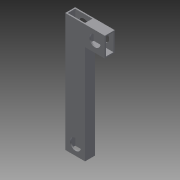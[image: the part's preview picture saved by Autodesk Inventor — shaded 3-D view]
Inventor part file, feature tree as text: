
AUTODESK INVENTOR PART (.ipt)
format: ipt  version: 2016 (Build 200138000, 138)  size: 128,000 bytes
history: native  units: in
note: dims shown in document units (in); Inventor stores cm internally (conversion verified against a paired STEP export)
features: extrude x5, sketch x5
ambient origin geometry x8: Origin, YZ Plane, XZ Plane, XY Plane, X Axis, Y Axis, Z Axis, Center Point
bodies: Solid1 (feature_tree)
feature tree (10):
  extrude  "Extrusion1"  Depth=1.0in
  extrude  "Extrusion2"  Depth=0.1253in
  extrude  "Extrusion3"  Depth=0.125in
  extrude  "Extrusion4"  Depth=2.0in
  extrude  "Extrusion5"  Depth=0.125in
  sketch  "Sketch1"  dims[d0=2.0in d1=1.0in]
  sketch  "Sketch2"  dims[d2=0.125in d3=0.1253in]
  sketch  "Sketch3"  dims[d4=0.125in d5=0.125in]
  sketch  "Sketch4"  dims[d6=12.0in d7=0.0in d8=2.0in]
  sketch  "Sketch5"  dims[d9=0.125in d10=0.125in d11=2.0in d12=0.0in d13=1.0in d14=1.125in d15=2.0in d16=0.0in d17=1.0in d18=1.125in d19=2.0in d20=0.0in d21=1.0in d22=1.125in d23=1.0in d24=1.0in d25=0.0in]
